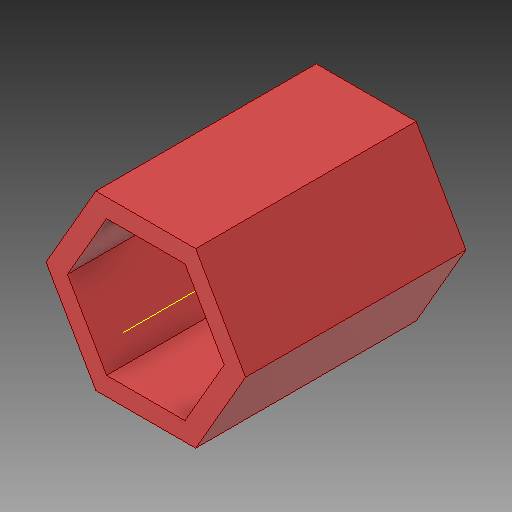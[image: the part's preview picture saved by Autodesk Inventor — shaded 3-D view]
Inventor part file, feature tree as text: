
AUTODESK INVENTOR PART (.ipt)
format: ipt  version: 2019.4 (Build 234330000, 330)  size: 103,936 bytes
history: native  units: in
note: dims shown in document units (in); Inventor stores cm internally (conversion verified against a paired STEP export)
features: extrude x1, sketch x1
ambient origin geometry x8: Origin, YZ Plane, XZ Plane, XY Plane, X Axis, Y Axis, Z Axis, Center Point
bodies: Solid1 (feature_tree)
feature tree (2):
  extrude  "Extrusion1"  Depth=0.385in
  sketch  "Sketch1"  dims[d0=0.49in d1=0.385in d2=0.625in d3=0.0in]
